# Revit family: Sink-American_Standard-Delancey-77SB30190.308
name_source: partatom
category: Plumbing Fixtures
revit_build: Autodesk Revit 2014 (Build: 20130308_1515(x64)
units: mm (PartAtom-declared; Revit-internal decimal feet)

## types (1)
- 77SB30190.308
    ADA Compliant = Yes
    Apron Height = 8 13/16"
    Assembly Code = D2010410
    Basin Shape = Rectangular
    Bowl Length = 15 3/8"
    Bowl Width = 26 1/16"
    CW Connection = Yes
    CWFU = 3
    Cold Water Connection Diameter = 1/2"
    Cold Water Connection Radius = 1/4"
    Cold Water Connection Width = 4"
    Default Elevation = 34"
    Description = Delancey Single Bowl Kitchen Sink
    Finish = Cast Iron-American Standard-308-Brilliant White
    HW Connection = Yes
    HWFU = 3
    Height = 8 11/16"
    Hot Water Connection Diameter = 1"
    Hot Water Connection Radius = 1/4"
    Hot Water Connection Width = 4"
    Installation Type = Undermount
    Length = 19"
    Manufacturer = American Standard
    Material = Cast Iron-American Standard-308-Brilliant White
    Model = 77SB30190.308
    Price = Prices may vary. Please consult Manufacturer Representative for most up-to-date price list.
    Type Comments = Minimum 33" (838mm) cabinet required
    URL = https://www.americanstandard-us.com
    Vent Connection = No
    WFU = 4
    Warranty Information = Limited Lifetime Warranty
    Waste Connection = Yes
    Waste Connection Diameter = 1 1/2"
    Waste Connection Offset = 11 13/16"
    Waste Connection Radius = 3/4"
    Waste Connection Width = 13 1/32"
    Width = 30"

## geometry (parser evidence)
native form markers: Sweep x1
no freeform markers — native parametric forms only
